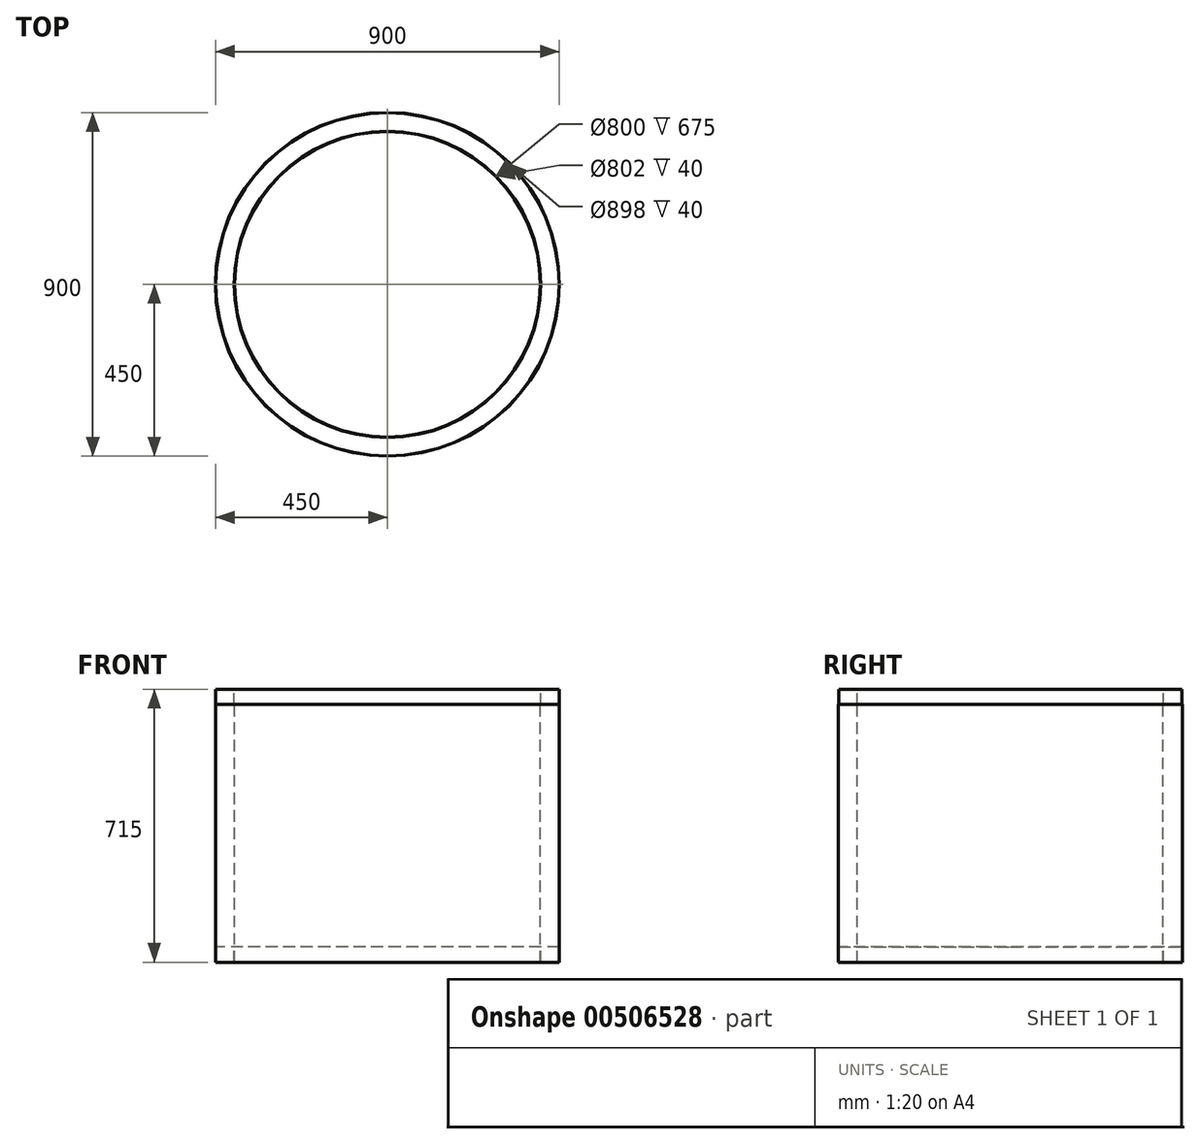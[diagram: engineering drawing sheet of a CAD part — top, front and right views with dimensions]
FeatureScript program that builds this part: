
annotation { "Feature Type Name" : "Feature", "Feature Type Description" : "" }
export const myFeature = defineFeature(function(context is Context, id is Id, definition is map)
    precondition{}
    {
        {
            var Q0;
            Q0=qCreatedBy(makeId("Front.planeOp"),FACE);
            var sketch = newSketch(context, id + "F0", { "sketchPlane" : qUnion([Q0])});
            skLineSegment(sketch, "E0", {"start": v(0, 74.87) * mm, "end": v(0, -73.71) * mm, "construction": true});
            skLineSegment(sketch, "E1", {"start": v(0, 374.84) * mm, "end": v(0, -528.94) * mm, "construction": true});
            skLineSegment(sketch, "E2", {"start": v(-400, -489.75) * mm, "end": v(-400, 185.25) * mm});
            skLineSegment(sketch, "E3", {"start": v(-400, 185.25) * mm, "end": v(-401, 185.25) * mm});
            skLineSegment(sketch, "E4", {"start": v(-401, 185.25) * mm, "end": v(-401, 225.25) * mm});
            skLineSegment(sketch, "E5", {"start": v(-401, 225.25) * mm, "end": v(-449, 225.25) * mm});
            skLineSegment(sketch, "E6", {"start": v(-449, 225.25) * mm, "end": v(-449, 185.25) * mm});
            skLineSegment(sketch, "E7", {"start": v(-449, 185.25) * mm, "end": v(-450, 185.25) * mm});
            skLineSegment(sketch, "E8", {"start": v(-450, 185.25) * mm, "end": v(-450, -489.75) * mm});
            skLineSegment(sketch, "E9", {"start": v(-450, -489.75) * mm, "end": v(-449, -489.75) * mm});
            skLineSegment(sketch, "E10", {"start": v(-449, -489.75) * mm, "end": v(-449, -449.75) * mm});
            skLineSegment(sketch, "E11", {"start": v(-449, -449.75) * mm, "end": v(-401, -449.75) * mm});
            skLineSegment(sketch, "E12", {"start": v(-401, -449.75) * mm, "end": v(-401, -489.75) * mm});
            skLineSegment(sketch, "E13", {"start": v(-401, -489.75) * mm, "end": v(-400, -489.75) * mm});
            skSolve(sketch);
        }
        {
            var Q0;
            Q0=qSketchRegion(id+"F0",true);
            var Q1;
            Q1=sQuery(id+"F0.wireOp",EDGE,"E1");
            revolve(context, id + "F1", {"entities" : qUnion([Q0]), "axis" : qUnion([Q1]), "revolveType" : RevolveType.FULL});
        }
    });
